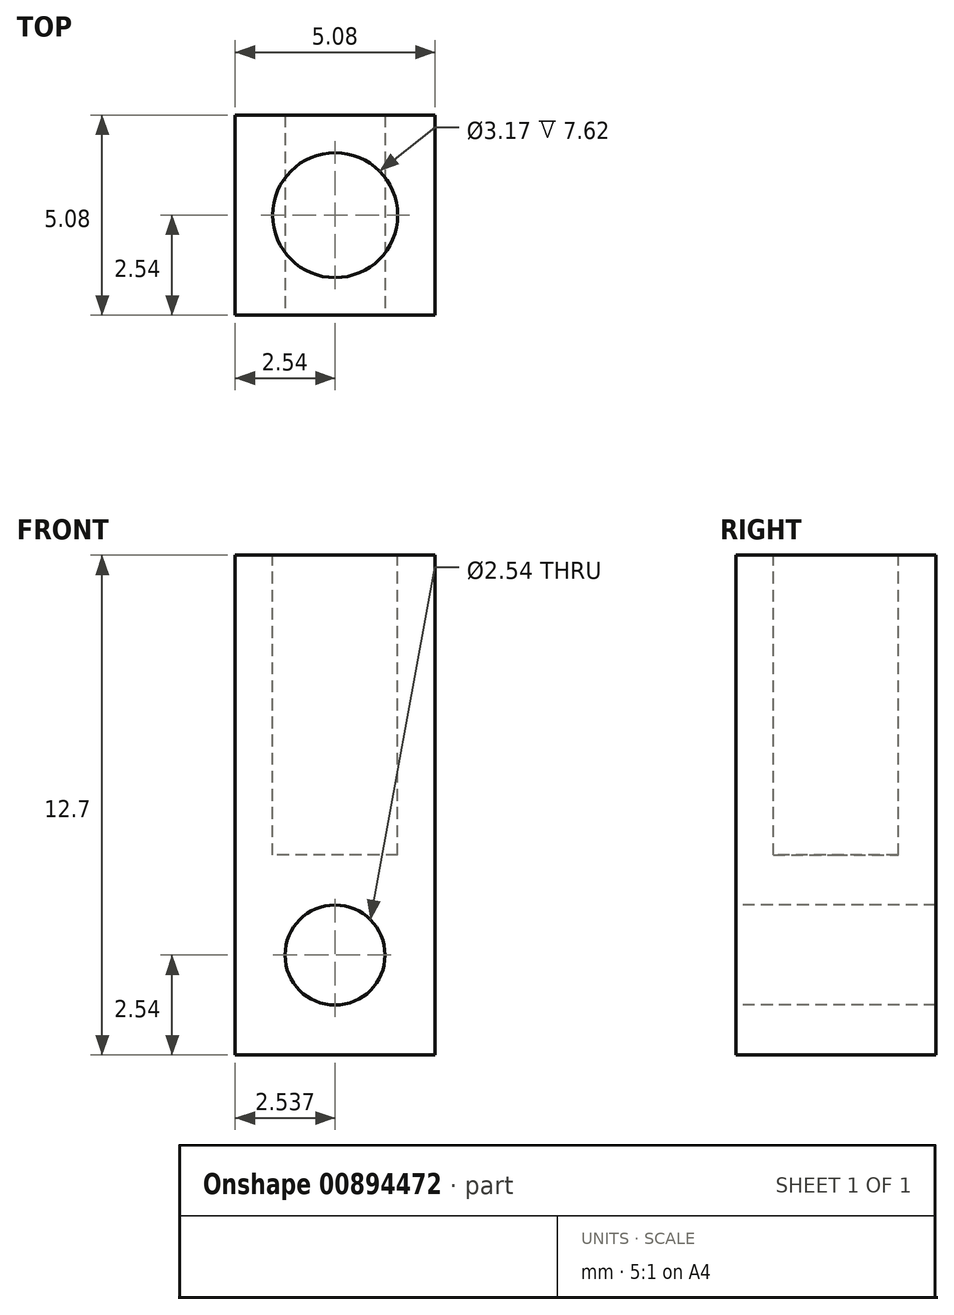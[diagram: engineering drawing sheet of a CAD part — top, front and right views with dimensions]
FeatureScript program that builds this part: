
annotation { "Feature Type Name" : "Feature", "Feature Type Description" : "" }
export const myFeature = defineFeature(function(context is Context, id is Id, definition is map)
    precondition{}
    {
        {
            var Q0;
            Q0=qCreatedBy(makeId("Top.planeOp"),FACE);
            var sketch = newSketch(context, id + "F0", { "sketchPlane" : qUnion([Q0])});
            skLineSegment(sketch, "E0.bottom", {"start": v(0, 0) * mm, "end": v(-5.08, 0) * mm});
            skLineSegment(sketch, "E0.top", {"start": v(0, 5.08) * mm, "end": v(-5.08, 5.08) * mm});
            skLineSegment(sketch, "E0.left", {"start": v(0, 0) * mm, "end": v(0, 5.08) * mm});
            skLineSegment(sketch, "E0.right", {"start": v(-5.08, 0) * mm, "end": v(-5.08, 5.08) * mm});
            skSolve(sketch);
        }
        {
            var Q0;
            Q0=makeQuery(id+"F0.imprint","IMPRINT",FACE,{"disambiguationData":[TD([[makeQuery(id+"F0.imprint","IMPRINT",EDGE,{"derivedFrom":sQuery(id+"F0.wireOp",EDGE,"E0.bottom")}),-1.0]])]});
            extrude(context, id + "F1", {"entities" : qUnion([Q0]), "depth" : 12.7 * mm, "offsetDistance" : 25.4 * mm});
        }
        {
            var Q0;
            Q0=makeQuery(id+"F1.opExtrude","SWEPT_FACE",FACE,{"disambiguationData":[OSD([sQuery(id+"F0.wireOp",EDGE,"E0.bottom")])]});
            var sketch = newSketch(context, id + "F2", { "sketchPlane" : qUnion([Q0])});
            skCircle(sketch, "E1", {"center": v(-2.54, 2.54) * mm, "radius": 1.27 * mm});
            skSolve(sketch);
        }
        {
            var Q0;
            Q0=makeQuery(id+"F2.imprint","IMPRINT",FACE,{"disambiguationData":[TD([[makeQuery(id+"F2.imprint","IMPRINT",EDGE,{"derivedFrom":sQuery(id+"F2.wireOp",EDGE,"E1")}),1.0]])]});
            extrude(context, id + "F3", {"entities" : qUnion([Q0]), "operationType" : NewBodyOperationType.REMOVE, "endBound" : BoundingType.THROUGH_ALL, "oppositeDirection" : true, "depth" : 25.4 * mm, "offsetDistance" : 25.4 * mm});
        }
        {
            var Q0;
            Q0=makeQuery(id+"F1.opExtrude","CAP_FACE",FACE,{"disambiguationData":[OSD([sQuery(id+"F0.wireOp",EDGE,"E0.bottom"),sQuery(id+"F0.wireOp",EDGE,"E0.top"),sQuery(id+"F0.wireOp",EDGE,"E0.left"),sQuery(id+"F0.wireOp",EDGE,"E0.right")])],"isStart":false});
            var sketch = newSketch(context, id + "F4", { "sketchPlane" : qUnion([Q0])});
            skCircle(sketch, "E2", {"center": v(-2.54, 2.54) * mm, "radius": 1.59 * mm});
            skSolve(sketch);
        }
        {
            var Q0;
            Q0=makeQuery(id+"F4.imprint","IMPRINT",FACE,{"disambiguationData":[TD([[makeQuery(id+"F4.imprint","IMPRINT",EDGE,{"derivedFrom":sQuery(id+"F4.wireOp",EDGE,"E2")}),1.0]])]});
            extrude(context, id + "F5", {"entities" : qUnion([Q0]), "operationType" : NewBodyOperationType.REMOVE, "oppositeDirection" : true, "depth" : 7.62 * mm, "offsetDistance" : 25.4 * mm});
        }
    });
